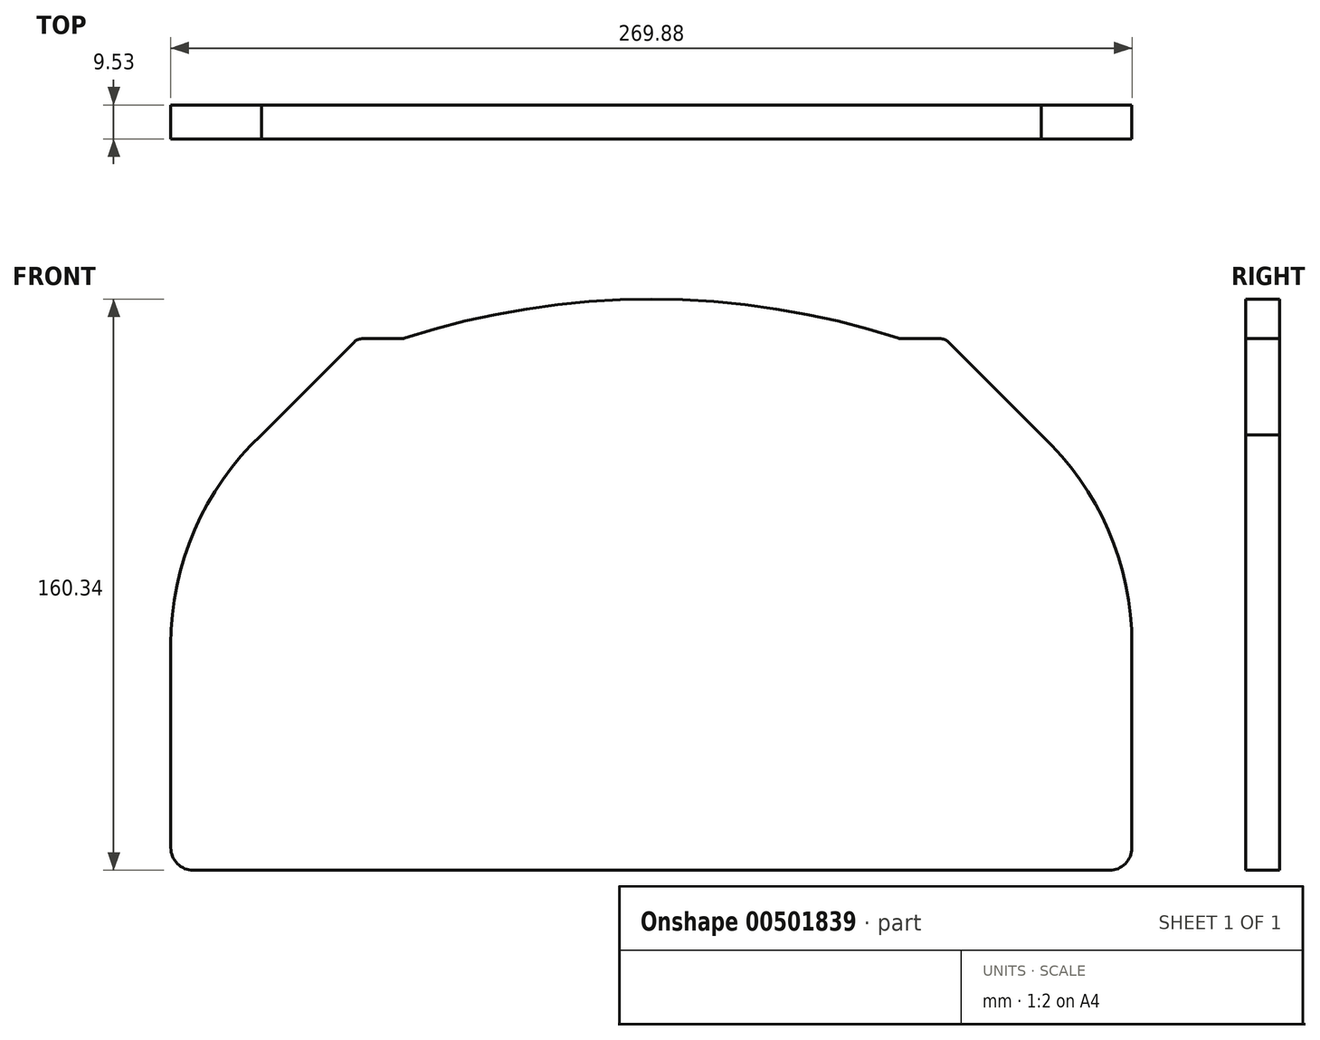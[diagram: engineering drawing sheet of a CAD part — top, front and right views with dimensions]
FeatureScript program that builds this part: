
annotation { "Feature Type Name" : "Feature", "Feature Type Description" : "" }
export const myFeature = defineFeature(function(context is Context, id is Id, definition is map)
    precondition{}
    {
        {
            var Q0;
            Q0=qCreatedBy(makeId("Front.planeOp"),FACE);
            var sketch = newSketch(context, id + "F0", { "sketchPlane" : qUnion([Q0])});
            skLineSegment(sketch, "E0", {"start": v(6.35, 0) * mm, "end": v(134.94, 0) * mm});
            skLineSegment(sketch, "E1", {"start": v(0, 6.35) * mm, "end": v(0, 63.5) * mm});
            skLineSegment(sketch, "E2", {"start": v(25.45, 122.28) * mm, "end": v(51.46, 148.3) * mm});
            skLineSegment(sketch, "E3", {"start": v(53.7, 149.23) * mm, "end": v(64.58, 149.23) * mm});
            skArc(sketch, "E4", {"start": v(0, 63.5) * mm, "mid": v(6.63, 95.53) * mm, "end": v(25.45, 122.28) * mm});
            skArc(sketch, "E5", {"start": v(134.94, 160.34) * mm, "mid": v(99.82, 157.58) * mm, "end": v(65.56, 149.38) * mm});
            skLineSegment(sketch, "E6", {"start": v(134.94, 160.34) * mm, "end": v(272.6, 160.34) * mm, "construction": true});
            skLineSegment(sketch, "E7", {"start": v(134.94, 160.34) * mm, "end": v(134.94, 0) * mm, "construction": true});
            skPoint(sketch, "E8.visualSharp", {"position": v(52.39, 149.23) * mm});
            skArc(sketch, "E8.filletArc", {"start": v(53.7, 149.23) * mm, "mid": v(52.49, 148.98) * mm, "end": v(51.46, 148.3) * mm});
            skPoint(sketch, "E9.visualSharp", {"position": v(65.09, 149.23) * mm});
            skArc(sketch, "E9.filletArc", {"start": v(64.58, 149.23) * mm, "mid": v(65.08, 149.26) * mm, "end": v(65.56, 149.38) * mm});
            skPoint(sketch, "E10.visualSharp", {"position": v(0, 0) * mm});
            skArc(sketch, "E10.filletArc", {"start": v(0, 6.35) * mm, "mid": v(1.86, 1.86) * mm, "end": v(6.35, 0) * mm});
            skArc(sketch, "E11.MirrorCS", {"start": v(134.94, 160.34) * mm, "mid": v(170.05, 157.58) * mm, "end": v(204.31, 149.38) * mm});
            skLineSegment(sketch, "E12.MirrorCS", {"start": v(244.43, 122.28) * mm, "end": v(218.42, 148.3) * mm});
            skLineSegment(sketch, "E13.MirrorCS", {"start": v(216.17, 149.23) * mm, "end": v(205.3, 149.23) * mm});
            skArc(sketch, "E14.MirrorCS", {"start": v(205.3, 149.23) * mm, "mid": v(204.8, 149.26) * mm, "end": v(204.31, 149.38) * mm});
            skArc(sketch, "E15.MirrorCS", {"start": v(216.17, 149.23) * mm, "mid": v(217.39, 148.98) * mm, "end": v(218.42, 148.3) * mm});
            skArc(sketch, "E16.MirrorCS", {"start": v(269.88, 63.5) * mm, "mid": v(263.24, 95.53) * mm, "end": v(244.43, 122.28) * mm});
            skLineSegment(sketch, "E17.MirrorCS", {"start": v(269.88, 6.35) * mm, "end": v(269.88, 63.5) * mm});
            skLineSegment(sketch, "E18.MirrorCS", {"start": v(263.53, 0) * mm, "end": v(134.94, 0) * mm});
            skArc(sketch, "E19.MirrorCS", {"start": v(269.88, 6.35) * mm, "mid": v(268.02, 1.86) * mm, "end": v(263.53, 0) * mm});
            skSolve(sketch);
        }
        {
            var Q0;
            Q0 = qSketchRegion(id + "F0", true);
            extrude(context, id + "F1", {"entities" : qUnion([Q0]), "depth" : 9.52 * mm});
        }
    });
